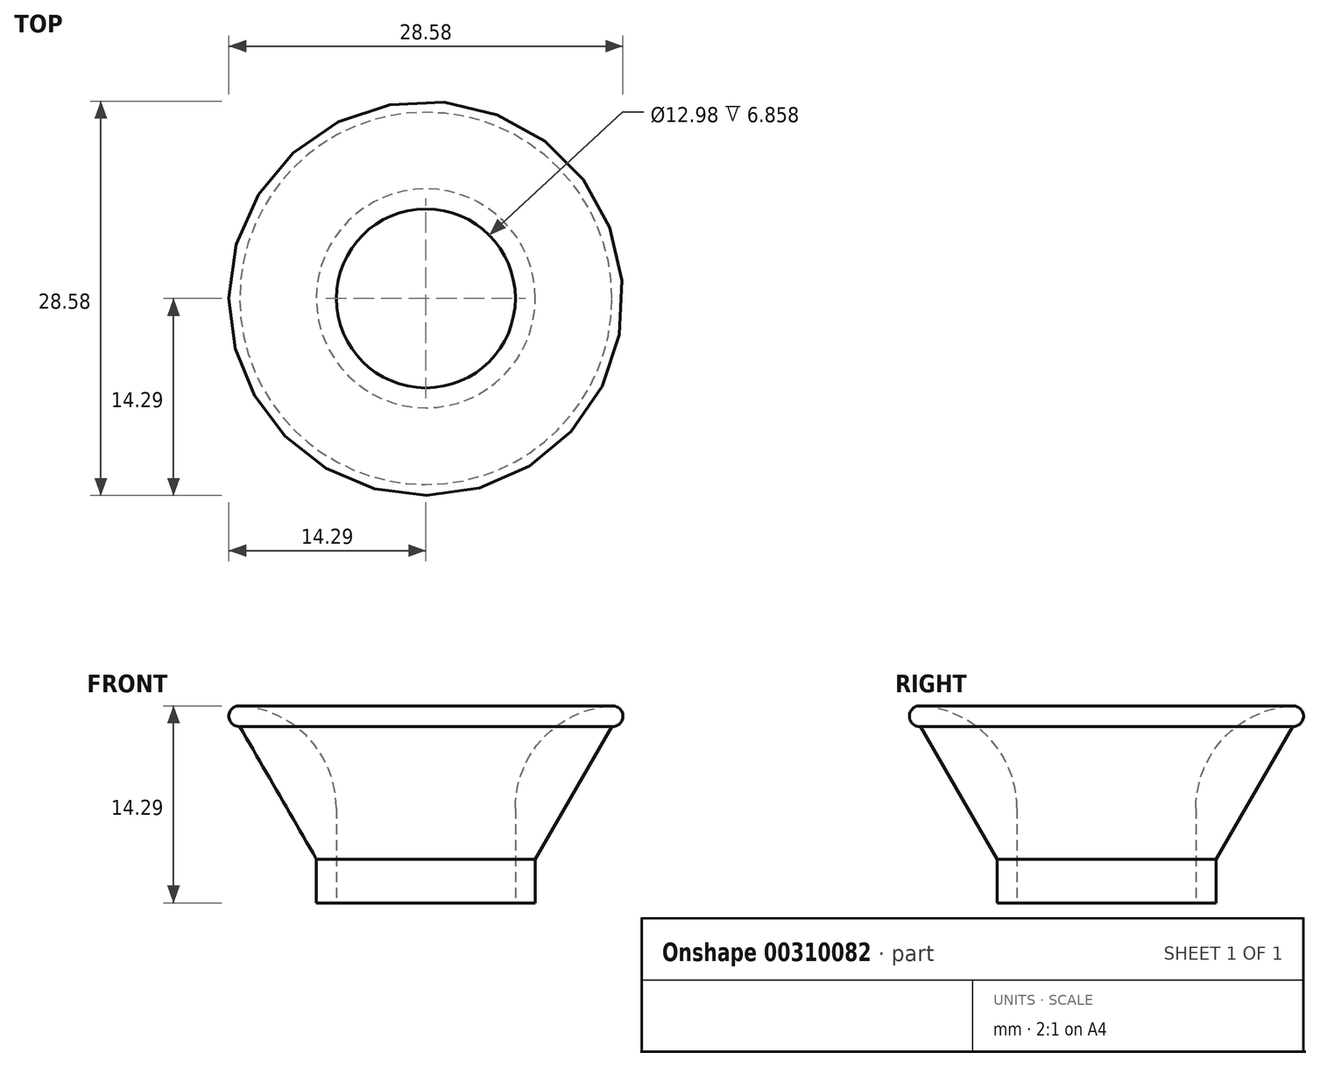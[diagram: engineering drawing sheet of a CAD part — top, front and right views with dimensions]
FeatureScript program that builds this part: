
annotation { "Feature Type Name" : "Feature", "Feature Type Description" : "" }
export const myFeature = defineFeature(function(context is Context, id is Id, definition is map)
    precondition{}
    {
        {
            var Q0;
            Q0=qCreatedBy(makeId("Front.planeOp"),FACE);
            var sketch = newSketch(context, id + "F0", { "sketchPlane" : qUnion([Q0])});
            skLineSegment(sketch, "E0", {"start": v(0, 0) * mm, "end": v(0, 11.14) * mm, "construction": true});
            skLineSegment(sketch, "E1", {"start": v(6.49, 0) * mm, "end": v(6.49, 6.86) * mm});
            skLineSegment(sketch, "E2", {"start": v(6.49, 0) * mm, "end": v(7.94, 0) * mm});
            skLineSegment(sketch, "E3", {"start": v(7.94, 0) * mm, "end": v(7.94, 3.17) * mm});
            skLineSegment(sketch, "E4", {"start": v(7.94, 3.17) * mm, "end": v(13.5, 12.79) * mm});
            skArc(sketch, "E5", {"start": v(13.5, 14.29) * mm, "mid": v(8.52, 11.96) * mm, "end": v(6.49, 6.86) * mm});
            skLineSegment(sketch, "E6", {"start": v(0, 0) * mm, "end": v(6.49, 0) * mm, "construction": true});
            skArc(sketch, "E7", {"start": v(13.5, 12.79) * mm, "mid": v(14.29, 13.54) * mm, "end": v(13.5, 14.29) * mm});
            skSolve(sketch);
        }
        {
            var Q0;
            Q0=makeQuery(id+"F0.imprint","IMPRINT",FACE,{"disambiguationData":[TD([[makeQuery(id+"F0.imprint","IMPRINT",EDGE,{"derivedFrom":sQuery(id+"F0.wireOp",EDGE,"E1")}),-1.0]])]});
            var Q1;
            Q1=sQuery(id+"F0.wireOp",EDGE,"E0");
            revolve(context, id + "F1", {"entities" : qUnion([Q0]), "axis" : qUnion([Q1]), "revolveType" : RevolveType.FULL});
        }
    });
